# Revit family: SE-0004-SQU-2-0
name_source: partatom
category: Curtain Panels
revit_build: Autodesk Revit 2015 (Build: 20140606_1530(x64)
units: mm (PartAtom-declared; Revit-internal decimal feet)

## types (25) — shared parameters
Analytic Construction = <None>
Sun-Control Material = Aluminum
Warning 2' = Label

## per-type parameters (varying)
| type | Angle |
| Right 90 - Left 112.5 | SE-0004-SQU-2-0 : Right 90 - Left 112.5 |
| Right 90 - Left 135 | SE-0004-SQU-2-0 : Right 90 - Left 135 |
| Right 112.5 - Left 90 | SE-0004-SQU-2-0 : Right 112.5 - Left 90 |
| Right 112.5 - Left 112.5 | SE-0004-SQU-2-0 : Right 112.5 - Left 112.5 |
| Right 112.5 - Left 135 | SE-0004-SQU-2-0 : Right 112.5 - Left 135 |
| Right 135 - Left 90 | SE-0004-SQU-2-0 : Right 135 - Left 90 |
| Right 135 - Left 112.5 | SE-0004-SQU-2-0 : Right 135 - Left 112.5 |
| Right 135 - Left 135 | SE-0004-SQU-2-0 : Right 135 - Left 135 |
| Right 45 - Left 45 | SE-0004-SQU-2-0 : Right 45 - Left 45 |
| Right 45 - Left 67.5 | SE-0004-SQU-2-0 : Right 45 - Left 67.5 |
| Right 45 - Left 90 | SE-0004-SQU-2-0 : Right 45 - Left 90 |
| Right 67.5 - Left 45 | SE-0004-SQU-2-0 : Right 67.5 - Left 45 |
| Right 67.5 - Left 67.5 | SE-0004-SQU-2-0 : Right 67.5 - Left 67.5 |
| Right 67.5 - Left 90 | SE-0004-SQU-2-0 : Right 67.5 - Left 90 |
| Right 90 - Left 45 | SE-0004-SQU-2-0 : Right 90 - Left 45 |
| Right 90 - Left 67.5 | SE-0004-SQU-2-0 : Right 90 - Left 67.5 |
| Right 45 - Left 112.5 | SE-0004-SQU-2-0 : Right 45 - Left 112.5 |
| Right 45 - Left 135 | SE-0004-SQU-2-0 : Right 45 - Left 135 |
| Right 67.5 - Left 112.5 | SE-0004-SQU-2-0 : Right 67.5 - Left 112.5 |
| Right 67.5 - Left 135 | SE-0004-SQU-2-0 : Right 67.5 - Left 135 |
| Right 112.5 - Left 45 | SE-0004-SQU-2-0 : Right 112.5 - Left 45 |
| Right 112.5 - Left 67.5 | SE-0004-SQU-2-0 : Right 112.5 - Left 67.5 |
| Right 135 - Left 45 | SE-0004-SQU-2-0 : Right 135 - Left 45 |
| Right 135 - Left 67.5 | SE-0004-SQU-2-0 : Right 135 - Left 67.5 |
| Right 90 - Left 90 | SE-0004-SQU-2-0 : Right 90 - Left 90 |

## geometry (parser evidence)
native form markers: Blend x6, Sweep x14
no freeform markers — native parametric forms only
